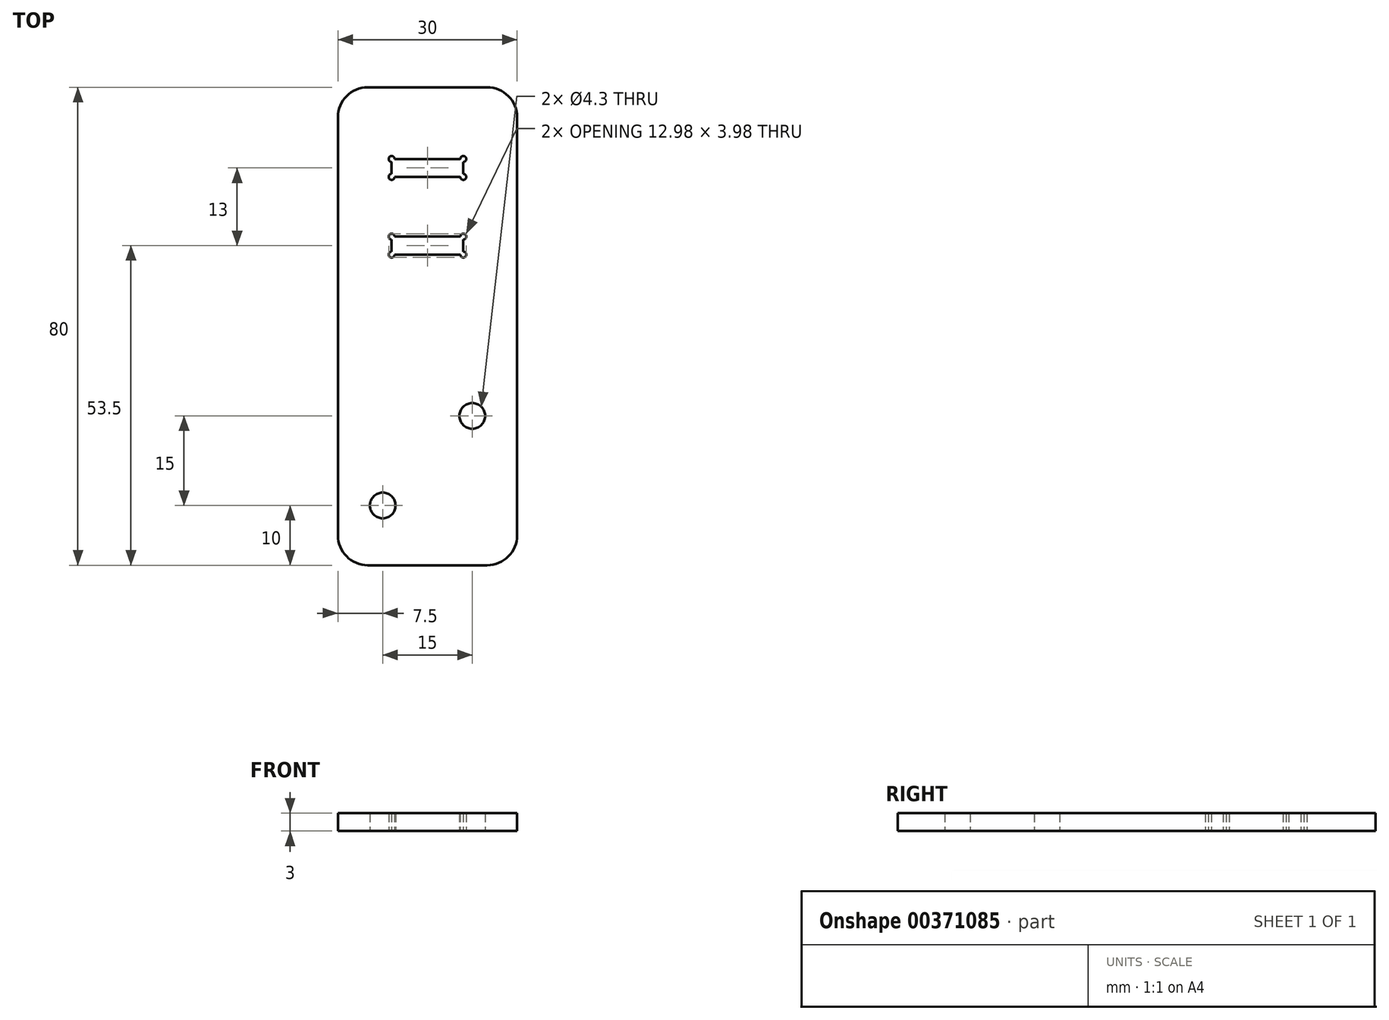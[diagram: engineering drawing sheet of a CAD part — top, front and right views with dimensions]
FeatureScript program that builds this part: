
annotation { "Feature Type Name" : "Feature", "Feature Type Description" : "" }
export const myFeature = defineFeature(function(context is Context, id is Id, definition is map)
    precondition{}
    {
        {
            var Q0;
            Q0=qCreatedBy(makeId("Top.planeOp"),FACE);
            var sketch = newSketch(context, id + "F0", { "sketchPlane" : qUnion([Q0])});
            skLineSegment(sketch, "E0.bottom", {"start": v(10, 40) * mm, "end": v(-10, 40) * mm});
            skLineSegment(sketch, "E0.top", {"start": v(10, -40) * mm, "end": v(-10, -40) * mm});
            skLineSegment(sketch, "E0.left", {"start": v(15, 35) * mm, "end": v(15, -35) * mm});
            skLineSegment(sketch, "E0.right", {"start": v(-15, 35) * mm, "end": v(-15, -35) * mm});
            skPoint(sketch, "E0.middle", {"position": v(0, 0) * mm});
            skPoint(sketch, "E1.visualSharp", {"position": v(-15, 40) * mm});
            skArc(sketch, "E1.filletArc", {"start": v(-10, 40) * mm, "mid": v(-13.54, 38.54) * mm, "end": v(-15, 35) * mm});
            skPoint(sketch, "E2.visualSharp", {"position": v(15, 40) * mm});
            skArc(sketch, "E2.filletArc", {"start": v(15, 35) * mm, "mid": v(13.54, 38.54) * mm, "end": v(10, 40) * mm});
            skPoint(sketch, "E3.visualSharp", {"position": v(15, -40) * mm});
            skArc(sketch, "E3.filletArc", {"start": v(10, -40) * mm, "mid": v(13.54, -38.54) * mm, "end": v(15, -35) * mm});
            skPoint(sketch, "E4.visualSharp", {"position": v(-15, -40) * mm});
            skArc(sketch, "E4.filletArc", {"start": v(-15, -35) * mm, "mid": v(-13.54, -38.54) * mm, "end": v(-10, -40) * mm});
            skLineSegment(sketch, "E5.bottom", {"start": v(6, 25) * mm, "end": v(-6, 25) * mm});
            skLineSegment(sketch, "E5.top", {"start": v(6, 28) * mm, "end": v(-6, 28) * mm});
            skLineSegment(sketch, "E5.left", {"start": v(6, 25) * mm, "end": v(6, 28) * mm});
            skLineSegment(sketch, "E5.right", {"start": v(-6, 25) * mm, "end": v(-6, 28) * mm});
            skPoint(sketch, "E5.middle", {"position": v(0, 26.5) * mm});
            skLineSegment(sketch, "E6.bottom", {"start": v(6, 12) * mm, "end": v(-6, 12) * mm});
            skLineSegment(sketch, "E6.top", {"start": v(6, 15) * mm, "end": v(-6, 15) * mm});
            skLineSegment(sketch, "E6.left", {"start": v(6, 12) * mm, "end": v(6, 15) * mm});
            skLineSegment(sketch, "E6.right", {"start": v(-6, 12) * mm, "end": v(-6, 15) * mm});
            skPoint(sketch, "E6.middle", {"position": v(0, 13.5) * mm});
            skCircle(sketch, "E7", {"center": v(-7.5, -30) * mm, "radius": 2.15 * mm});
            skCircle(sketch, "E8", {"center": v(7.5, -15) * mm, "radius": 2.15 * mm});
            skCircle(sketch, "E9", {"center": v(-6, 28) * mm, "radius": 0.5 * mm});
            skCircle(sketch, "E10", {"center": v(-6, 25) * mm, "radius": 0.5 * mm});
            skCircle(sketch, "E11", {"center": v(6, 28) * mm, "radius": 0.5 * mm});
            skCircle(sketch, "E12", {"center": v(6, 25) * mm, "radius": 0.5 * mm});
            skCircle(sketch, "E13", {"center": v(-6, 15) * mm, "radius": 0.5 * mm});
            skCircle(sketch, "E14", {"center": v(6, 15) * mm, "radius": 0.5 * mm});
            skCircle(sketch, "E15", {"center": v(6, 12) * mm, "radius": 0.5 * mm});
            skCircle(sketch, "E16", {"center": v(-6, 12) * mm, "radius": 0.5 * mm});
            skSolve(sketch);
        }
        {
            var Q0;
            Q0=makeQuery(id+"F0.imprint","IMPRINT",FACE,{"disambiguationData":[TD([[makeQuery(id+"F0.imprint","IMPRINT",EDGE,{"derivedFrom":sQuery(id+"F0.wireOp",EDGE,"E0.bottom")}),1.0]])]});
            extrude(context, id + "F1", {"entities" : qUnion([Q0]), "depth" : 3 * mm});
        }
    });
